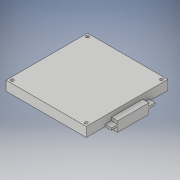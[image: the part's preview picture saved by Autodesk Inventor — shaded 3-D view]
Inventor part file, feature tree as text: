
AUTODESK INVENTOR PART (.ipt)
format: ipt  version: 2019 (Build 230136000, 136)  size: 137,728 bytes
history: native  units: mm
features: sketch x4, extrude x3, hole x1, plane x1
ambient origin geometry x8: Origin, YZ Plane, XZ Plane, XY Plane, X Axis, Y Axis, Z Axis, Center Point
bodies: Solid1 (feature_tree)
feature tree (9):
  extrude  "Extrusion1"  Depth=65.0mm
  extrude  "Extrusion2"  Depth=15.0mm
  extrude  "Extrusion3"  Depth=1.6mm TaperAngle=0.0deg
  hole  "Hole1"  [1 undecoded]
  plane  "Work Plane1"
  sketch  "Sketch1"  dims[d0=64.0mm d1=65.0mm]
  sketch  "Sketch2"  dims[d2=5.0mm d3=15.0mm]
  sketch  "Sketch3"  dims[d4=15.0mm d5=1.6mm d6=0.0mm]
  sketch  "Sketch4"  dims[d7=5.0mm d8=25.0mm d9=8.0mm d10=0.0mm d11=6.0mm d12=0.0mm d13=2.5mm d14=2.5mm d15=20.0mm d17=59.0mm d18=20.0mm d20=60.0mm d23=2.4mm d24=6.0mm d25=4.4mm d26=2.0mm d27=90.0deg d28=8.0mm d29=20.594885mm]
note: 1 required parameter value undecoded (feature->parameter linkage not recoverable at this tier; creation-order binding heuristic only, values carry confidence <= 0.55)
